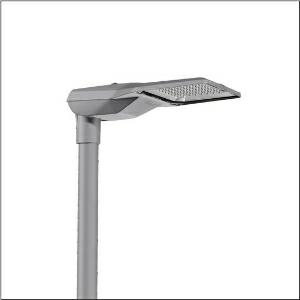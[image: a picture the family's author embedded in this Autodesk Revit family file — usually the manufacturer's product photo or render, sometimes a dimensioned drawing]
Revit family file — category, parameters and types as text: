
# Revit family: streetlight_sl_21_midi___st1_0a_5xe3d43s08mb_8ac5
name_source: partatom
category: Lighting Fixtures
units: mm (PartAtom-declared; Revit-internal decimal feet)

## family parameters
Cut with Voids When Loaded = No
Host = Face
Light Source = No
Part Type = Normal
Room Calculation Point = No
Round Connector Dimension = Use Diameter
Shared = No

## types (1)
- --- (1 x LED, 20180 lm, 147 W, 4000K)
    Apparent Load = 147 VA
    CIE Flux Codes = 37 72 97 100 100
    Color Rendering = 70
    Color Temperature = 4000K
    Default Elevation = 1800 mm
    Description = Streetlight SL 21 midi, mast luminaire, primary light control with lens, of PMMA, primary optical cover: cover, of toughened safety glass, transparent, light distribution: ST1.0a, light emission: direct distribution, primary light characteristic: asymmetric, installation type: side-entry, post-top, LED, High Power LED, rated luminous flux: 20.180lm, luminous efficacy: 137lm/W, light colour: 740, colour temperature: 4000K, control gear: D4i, control: overheat protection, constant luminous flux control, time-dependent luminous flux control, flexible luminous flux parameterisation, pre-setting: logarithmic dimming characteristic, mains connection: 230..240V, AC, 50/60Hz, start of lifetime: 147W, end of service life: 155W, reduction: 65W, luminaire housing, of diecast aluminium, powder-coated, Siteco® metallic grey (DB 702S), corrosivity category C5 mid according to DIN EN ISO 12944, please order mast flange separately, inclination adjustable: 0°, 5°, 10°, 15°, sealing non-destructively replaceable, multi-level sealing system, length: 644mm, width: 335mm, height: 110mm, mast flange for spigot size: 42mm (side-entry): 5XC10008XM4, 60/48mm (side-entry/post-top): 5XC10108XM2, 76/60mm (side-entry/post-top): 5XC10108XM1, mounting height: 4..8m, Smart Interface above, protection rating (complete): IP66, insulation class (complete): insulation class II (safety insulation), certification: CE, ENEC, ENEC+, VDE, impact resistance: IK10, permissible operating ambient temperature for outdoor applications: -40..+50°C, standard-compliant lighting for roads and squares, packaging unit: 1 piece

Light Distribution: ST1.0a
    Height = 111 mm
    Lamp = 1 x LED
    Lamp Light Flux = 20180 lm
    Lamp Power = 147 W
    Lamp count = 1
    Length = 644 mm
    Luminous efficacy = 137 lm/W
    Manufacturer = Siteco
    ModVariant = No
    Model = 5XE3D43S08MB
    Number of Poles = 1
    OnlyDefault = Yes
    Power Factor = 1
    Product Name = Streetlight SL 21 midi | ST1.0a
    Product group = mast luminaire | pylon top
    ProductGroupID = 6100
    Protection Class = Protection class II
    Protection Degree = IP 66
    RLX_Detail_Level = 1
    RLX_Emergency_Light_Flux = 0 lm
    RLX_Emergency_Type = 0
    RLX_Emergency_Type_DB = No
    RlxData = <blob elided: 26825 chars, md5=f7498431>
    Socket = socket
    Standby Power = 0 W
    System Light Flux = 20180 lm
    System Power = 147 W
    Type Comments = factory setting: luminous flux: 100 % | dim-lin: 254 | 750 mA
    Type Image = l_1004302.jpg
    URL = http://relux.com
    VarID = @adj_189304
    Voltage = 0 V
    Weight = 0.00 kg
    Width = 336 mm

## geometry (parser evidence)
native form markers: Blend x4, Sweep x12
no freeform markers — native parametric forms only
